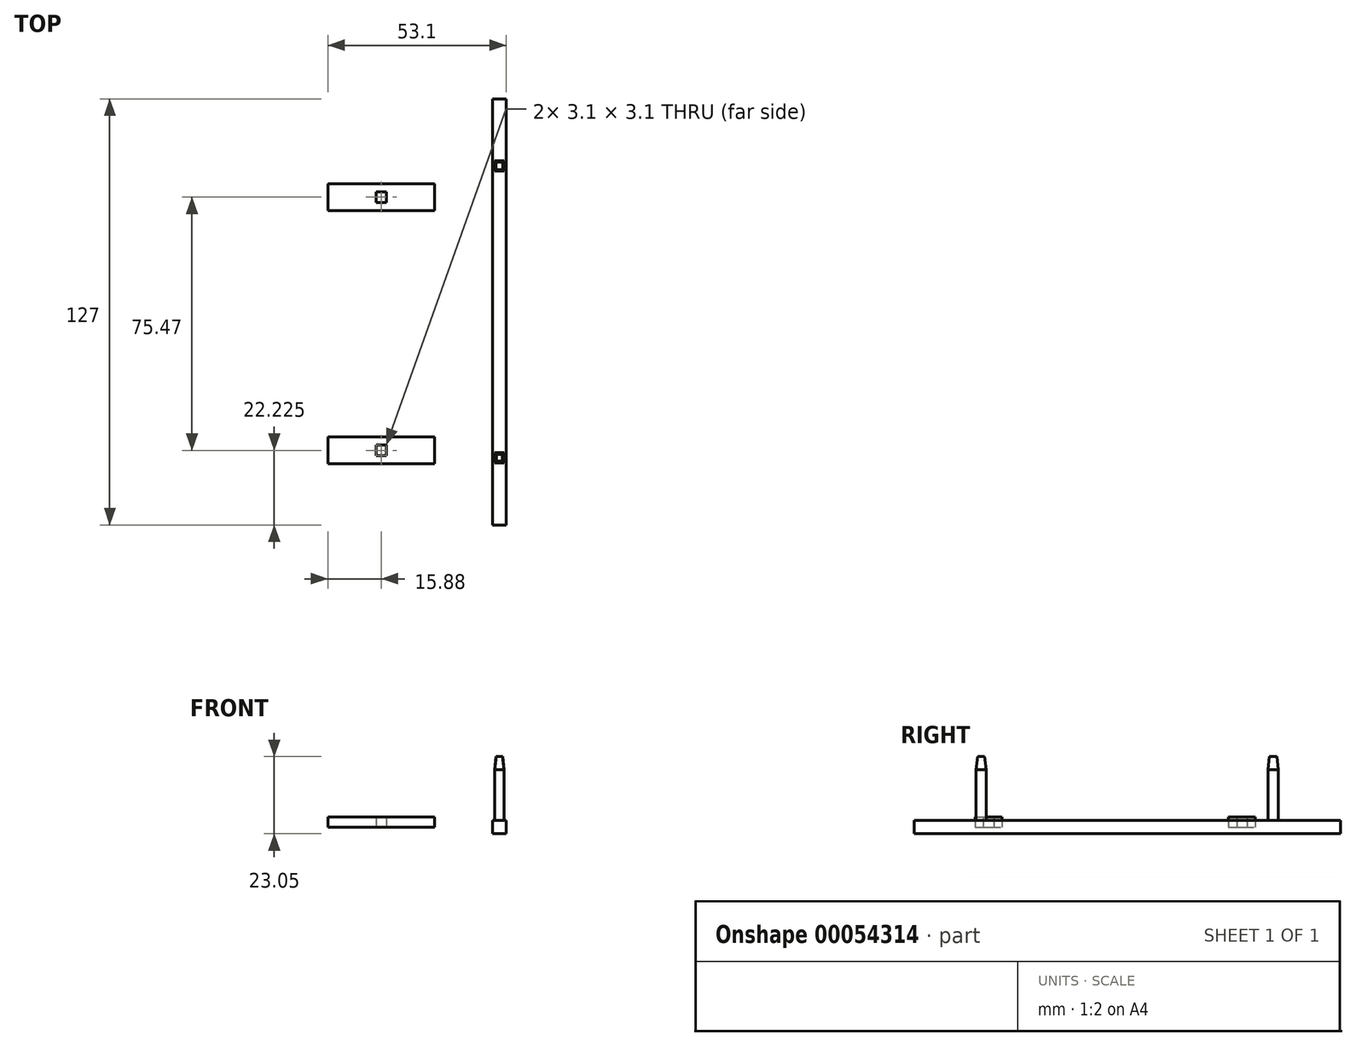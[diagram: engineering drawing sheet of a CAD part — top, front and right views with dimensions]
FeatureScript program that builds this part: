
annotation { "Feature Type Name" : "Feature", "Feature Type Description" : "" }
export const myFeature = defineFeature(function(context is Context, id is Id, definition is map)
    precondition{}
    {
        {
            var Q0;
            Q0=qCreatedBy(makeId("Front.planeOp"),FACE);
            var sketch = newSketch(context, id + "F0", { "sketchPlane" : qUnion([Q0])});
            skLineSegment(sketch, "E0.rect.bottom", {"start": v(2, 2) * mm, "end": v(-2, 2) * mm});
            skLineSegment(sketch, "E0.rect.top", {"start": v(2, -2) * mm, "end": v(-2, -2) * mm});
            skLineSegment(sketch, "E0.rect.left", {"start": v(2, 2) * mm, "end": v(2, -2) * mm});
            skLineSegment(sketch, "E0.rect.right", {"start": v(-2, 2) * mm, "end": v(-2, -2) * mm});
            skPoint(sketch, "E0.rect.middle", {"position": v(0, 0) * mm});
            skSolve(sketch);
        }
        {
            var Q0;
            Q0=makeQuery(id+"F0.imprint","IMPRINT",FACE,{"disambiguationData":[TD([[makeQuery(id+"F0.imprint","IMPRINT",EDGE,{"derivedFrom":sQuery(id+"F0.wireOp",EDGE,"E0.rect.bottom")}),1.0]])]});
            extrude(context, id + "F1", {"entities" : qUnion([Q0]), "oppositeDirection" : true, "depth" : 127 * mm});
        }
        {
            var Q0;
            Q0=makeQuery(id+"F1.opExtrude","SWEPT_FACE",FACE,{"disambiguationData":[OSD([sQuery(id+"F0.wireOp",EDGE,"E0.rect.bottom")])]});
            var sketch = newSketch(context, id + "F2", { "sketchPlane" : qUnion([Q0])});
            skLineSegment(sketch, "E1.rect.bottom", {"start": v(1.38, 21.5) * mm, "end": v(-1.38, 21.5) * mm});
            skLineSegment(sketch, "E1.rect.top", {"start": v(1.38, 18.5) * mm, "end": v(-1.38, 18.5) * mm});
            skLineSegment(sketch, "E1.rect.left", {"start": v(1.38, 21.5) * mm, "end": v(1.38, 18.5) * mm});
            skLineSegment(sketch, "E1.rect.right", {"start": v(-1.38, 21.5) * mm, "end": v(-1.38, 18.5) * mm});
            skPoint(sketch, "E1.rect.middle", {"position": v(0, 20) * mm});
            skPoint(sketch, "E2", {"position": v(0, 127) * mm});
            skLineSegment(sketch, "E3.rect.bottom", {"start": v(-1.38, 108.5) * mm, "end": v(1.38, 108.5) * mm});
            skLineSegment(sketch, "E3.rect.top", {"start": v(-1.38, 105.5) * mm, "end": v(1.38, 105.5) * mm});
            skLineSegment(sketch, "E3.rect.left", {"start": v(-1.38, 108.5) * mm, "end": v(-1.38, 105.5) * mm});
            skLineSegment(sketch, "E3.rect.right", {"start": v(1.38, 108.5) * mm, "end": v(1.38, 105.5) * mm});
            skPoint(sketch, "E3.rect.middle", {"position": v(0, 107) * mm});
            skSolve(sketch);
        }
        {
            var Q0;
            Q0=makeQuery(id+"F2.imprint","IMPRINT",FACE,{"disambiguationData":[TD([[makeQuery(id+"F2.imprint","IMPRINT",EDGE,{"derivedFrom":sQuery(id+"F2.wireOp",EDGE,"E3.rect.bottom")}),-1.0]])]});
            var Q1;
            Q1=makeQuery(id+"F2.imprint","IMPRINT",FACE,{"disambiguationData":[TD([[makeQuery(id+"F2.imprint","IMPRINT",EDGE,{"derivedFrom":sQuery(id+"F2.wireOp",EDGE,"E1.rect.bottom")}),1.0]])]});
            extrude(context, id + "F3", {"entities" : qUnion([Q0, Q1]), "operationType" : NewBodyOperationType.ADD, "depth" : 19.05 * mm});
        }
        {
            var Q0;
            Q0=makeQuery(id+"F3.opExtrude","CAP_EDGE",EDGE,{"disambiguationData":[OSD([sQuery(id+"F2.wireOp",EDGE,"E3.rect.right")])],"isStart":false});
            var Q1;
            Q1=makeQuery(id+"F3.opExtrude","CAP_EDGE",EDGE,{"disambiguationData":[OSD([sQuery(id+"F2.wireOp",EDGE,"E3.rect.bottom")])],"isStart":false});
            var Q2;
            Q2=makeQuery(id+"F3.opExtrude","CAP_EDGE",EDGE,{"disambiguationData":[OSD([sQuery(id+"F2.wireOp",EDGE,"E3.rect.left")])],"isStart":false});
            var Q3;
            Q3=makeQuery(id+"F3.opExtrude","CAP_EDGE",EDGE,{"disambiguationData":[OSD([sQuery(id+"F2.wireOp",EDGE,"E3.rect.top")])],"isStart":false});
            chamfer(context, id + "F4", {"entities" : qUnion([Q0, Q1, Q2, Q3]), "chamferType" : ChamferType.TWO_OFFSETS, "width1" : 4 * mm, "oppositeDirection" : false, "width2" : .4 * mm, "tangentPropagation" : true});
        }
        {
            var Q0;
            Q0=makeQuery(id+"F3.opExtrude","CAP_EDGE",EDGE,{"disambiguationData":[OSD([sQuery(id+"F2.wireOp",EDGE,"E1.rect.top")])],"isStart":false});
            var Q1;
            Q1=makeQuery(id+"F3.opExtrude","CAP_EDGE",EDGE,{"disambiguationData":[OSD([sQuery(id+"F2.wireOp",EDGE,"E1.rect.left")])],"isStart":false});
            var Q2;
            Q2=makeQuery(id+"F3.opExtrude","CAP_EDGE",EDGE,{"disambiguationData":[OSD([sQuery(id+"F2.wireOp",EDGE,"E1.rect.right")])],"isStart":false});
            var Q3;
            Q3=makeQuery(id+"F3.opExtrude","CAP_EDGE",EDGE,{"disambiguationData":[OSD([sQuery(id+"F2.wireOp",EDGE,"E1.rect.bottom")])],"isStart":false});
            chamfer(context, id + "F5", {"entities" : qUnion([Q0, Q1, Q2, Q3]), "chamferType" : ChamferType.TWO_OFFSETS, "width1" : 4 * mm, "oppositeDirection" : false, "width2" : .5 * mm, "tangentPropagation" : true});
        }
        {
            var Q0;
            Q0=qCreatedBy(makeId("Top.planeOp"),FACE);
            var sketch = newSketch(context, id + "F6", { "sketchPlane" : qUnion([Q0])});
            skLineSegment(sketch, "E4.rect.bottom", {"start": v(-19.35, 18.22) * mm, "end": v(-51.1, 18.22) * mm});
            skLineSegment(sketch, "E4.rect.top", {"start": v(-19.35, 26.22) * mm, "end": v(-51.1, 26.22) * mm});
            skLineSegment(sketch, "E4.rect.left", {"start": v(-19.35, 18.22) * mm, "end": v(-19.35, 26.22) * mm});
            skLineSegment(sketch, "E4.rect.right", {"start": v(-51.1, 18.22) * mm, "end": v(-51.1, 26.22) * mm});
            skPoint(sketch, "E4.rect.middle", {"position": v(-35.22, 22.22) * mm});
            skLineSegment(sketch, "E5.rect.bottom", {"start": v(-19.35, 93.7) * mm, "end": v(-51.1, 93.7) * mm});
            skLineSegment(sketch, "E5.rect.top", {"start": v(-19.35, 101.7) * mm, "end": v(-51.1, 101.7) * mm});
            skLineSegment(sketch, "E5.rect.left", {"start": v(-19.35, 93.7) * mm, "end": v(-19.35, 101.7) * mm});
            skLineSegment(sketch, "E5.rect.right", {"start": v(-51.1, 93.7) * mm, "end": v(-51.1, 101.7) * mm});
            skPoint(sketch, "E5.rect.middle", {"position": v(-35.22, 97.7) * mm});
            skLineSegment(sketch, "E6.rect.bottom", {"start": v(-33.67, 20.67) * mm, "end": v(-36.77, 20.67) * mm});
            skLineSegment(sketch, "E6.rect.top", {"start": v(-33.67, 23.77) * mm, "end": v(-36.77, 23.77) * mm});
            skLineSegment(sketch, "E6.rect.left", {"start": v(-33.67, 20.67) * mm, "end": v(-33.67, 23.77) * mm});
            skLineSegment(sketch, "E6.rect.right", {"start": v(-36.77, 20.67) * mm, "end": v(-36.77, 23.77) * mm});
            skLineSegment(sketch, "E7.rect.bottom", {"start": v(-33.67, 96.15) * mm, "end": v(-36.77, 96.15) * mm});
            skLineSegment(sketch, "E7.rect.top", {"start": v(-33.67, 99.25) * mm, "end": v(-36.77, 99.25) * mm});
            skLineSegment(sketch, "E7.rect.left", {"start": v(-33.67, 96.15) * mm, "end": v(-33.67, 99.25) * mm});
            skLineSegment(sketch, "E7.rect.right", {"start": v(-36.77, 96.15) * mm, "end": v(-36.77, 99.25) * mm});
            skSolve(sketch);
        }
        {
            var Q0;
            Q0=makeQuery(id+"F6.imprint","IMPRINT",FACE,{"disambiguationData":[TD([[makeQuery(id+"F6.imprint","IMPRINT",EDGE,{"derivedFrom":sQuery(id+"F6.wireOp",EDGE,"E5.rect.bottom")}),-1.0]])]});
            var Q1;
            Q1=makeQuery(id+"F6.imprint","IMPRINT",FACE,{"disambiguationData":[TD([[makeQuery(id+"F6.imprint","IMPRINT",EDGE,{"derivedFrom":sQuery(id+"F6.wireOp",EDGE,"E4.rect.bottom")}),-1.0]])]});
            extrude(context, id + "F7", {"entities" : qUnion([Q0, Q1]), "depth" : 3 * mm});
        }
    });
